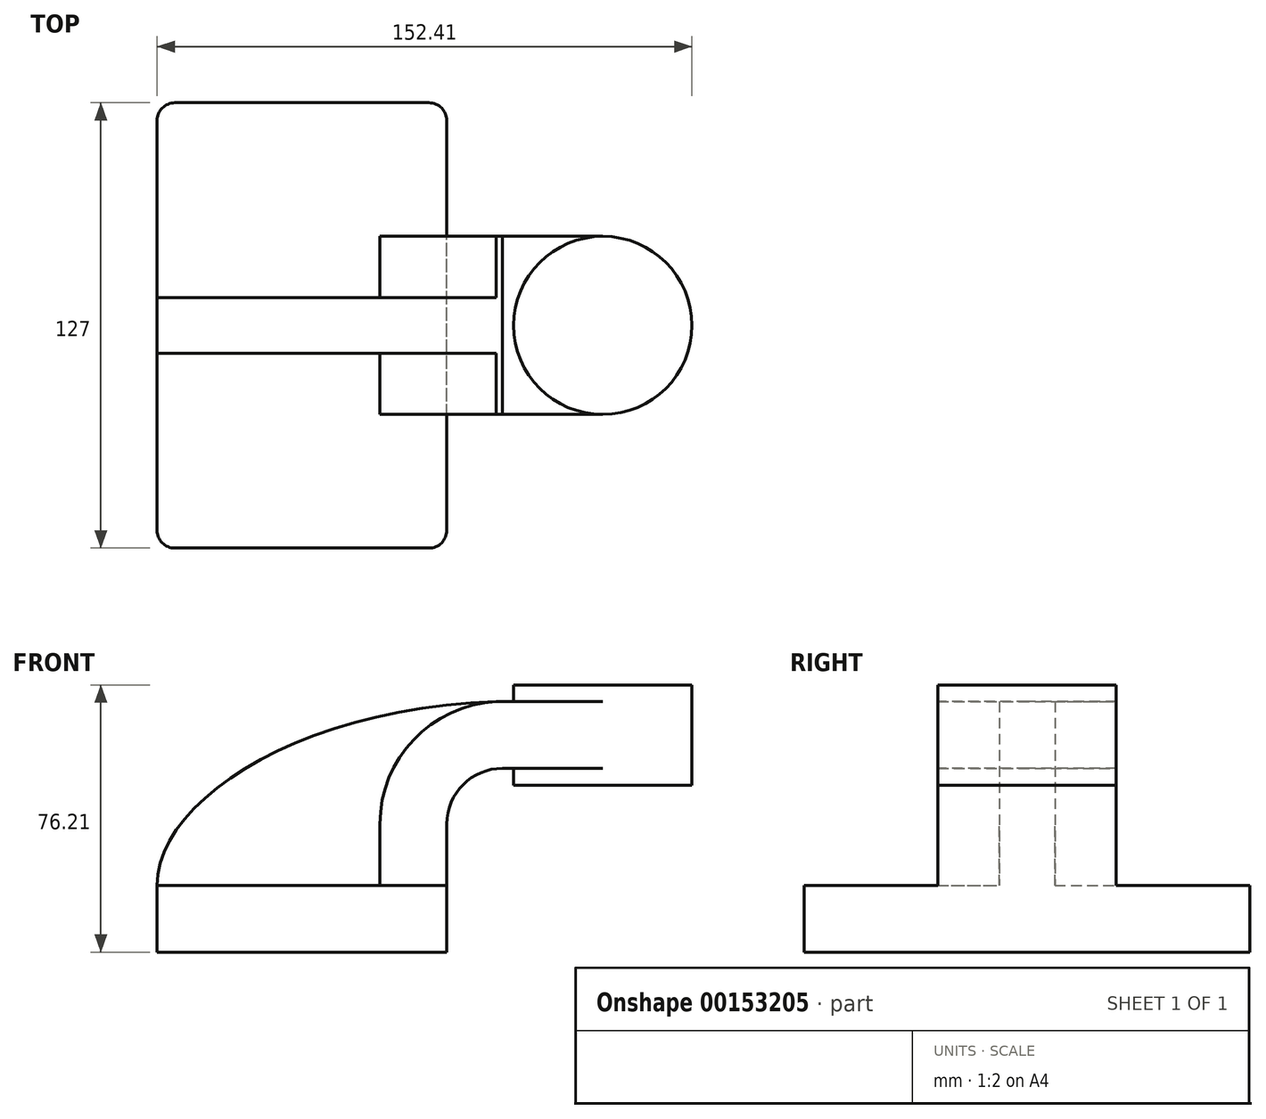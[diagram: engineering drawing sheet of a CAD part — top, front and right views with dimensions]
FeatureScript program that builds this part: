
annotation { "Feature Type Name" : "Feature", "Feature Type Description" : "" }
export const myFeature = defineFeature(function(context is Context, id is Id, definition is map)
    precondition{}
    {
        {
            var Q0;
            Q0=qCreatedBy(makeId("Front.planeOp"),FACE);
            var sketch = newSketch(context, id + "F0", { "sketchPlane" : qUnion([Q0])});
            skLineSegment(sketch, "E0.bottom", {"start": v(41.27, 9.53) * mm, "end": v(-41.28, 9.53) * mm});
            skLineSegment(sketch, "E0.top", {"start": v(41.28, -9.52) * mm, "end": v(-41.27, -9.52) * mm});
            skLineSegment(sketch, "E0.left", {"start": v(41.28, 9.53) * mm, "end": v(41.28, -9.52) * mm});
            skLineSegment(sketch, "E0.right", {"start": v(-41.28, 9.53) * mm, "end": v(-41.27, -9.52) * mm});
            skPoint(sketch, "E0.middle", {"position": v(0, 0) * mm});
            skLineSegment(sketch, "E1.bottom", {"start": v(60.33, 38.1) * mm, "end": v(111.13, 38.1) * mm});
            skLineSegment(sketch, "E1.top", {"start": v(60.33, 66.68) * mm, "end": v(111.13, 66.68) * mm});
            skLineSegment(sketch, "E1.left", {"start": v(60.33, 38.1) * mm, "end": v(60.33, 66.67) * mm});
            skLineSegment(sketch, "E1.right", {"start": v(111.13, 38.1) * mm, "end": v(111.13, 66.68) * mm});
            skPoint(sketch, "E1.middle", {"position": v(85.73, 52.39) * mm});
            skLineSegment(sketch, "E2", {"start": v(41.27, 9.53) * mm, "end": v(41.27, 27) * mm});
            skArc(sketch, "E3", {"start": v(41.28, 27) * mm, "mid": v(45.92, 38.23) * mm, "end": v(57.15, 42.88) * mm});
            skLineSegment(sketch, "E4", {"start": v(57.15, 42.88) * mm, "end": v(85.73, 42.88) * mm});
            skLineSegment(sketch, "E5.0", {"start": v(57.15, 61.93) * mm, "end": v(85.73, 61.93) * mm});
            skArc(sketch, "E5.1", {"start": v(22.23, 27) * mm, "mid": v(32.45, 51.7) * mm, "end": v(57.15, 61.93) * mm});
            skLineSegment(sketch, "E5.2", {"start": v(22.22, 9.53) * mm, "end": v(22.22, 27) * mm});
            skFitSpline(sketch, "E6", {"points": [v(57.15, 61.93) * mm, v(-41.28, 9.53) * mm], "startDerivative": vector(-171.45, -3.59) * mm, "endDerivative": vector(0, -73) * mm});
            skLineSegment(sketch, "E7", {"start": v(85.73, 38.1) * mm, "end": v(85.73, 66.68) * mm});
            skSolve(sketch);
        }
        {
            var Q0;
            Q0=makeQuery(id+"F0.imprint","IMPRINT",FACE,{"disambiguationData":[TD([[makeQuery(id+"F0.imprint","IMPRINT",EDGE,{"derivedFrom":sQuery(id+"F0.wireOp",EDGE,"E0.top")}),-1.0]])]});
            extrude(context, id + "F1", {"entities" : qUnion([Q0]), "endBound" : BoundingType.SYMMETRIC, "depth" : 127 * mm});
        }
        {
            var Q0;
            {var subQ1=sQuery(id+"F0.wireOp",EDGE,"E2");Q0=makeQuery(id+"F0.imprint","IMPRINT",FACE,{"disambiguationData":[TD([[makeQuery(id+"F0.imprint","IMPRINT",EDGE,{"derivedFrom":subQ1}),1.0]])]});}
            extrude(context, id + "F2", {"entities" : qUnion([Q0]), "operationType" : NewBodyOperationType.ADD, "endBound" : BoundingType.SYMMETRIC, "depth" : 50.8 * mm});
        }
        {
            var Q0;
            {var subQ3=sQuery(id+"F0.wireOp",EDGE,"E5.2");Q0=makeQuery(id+"F0.imprint","IMPRINT",FACE,{"disambiguationData":[TD([[makeQuery(id+"F0.imprint","IMPRINT",EDGE,{"derivedFrom":subQ3}),1.0]])]});}
            extrude(context, id + "F3", {"entities" : qUnion([Q0]), "operationType" : NewBodyOperationType.ADD, "endBound" : BoundingType.SYMMETRIC, "depth" : 15.88 * mm});
        }
        {
            var Q0;
            {var subQ0=sQuery(id+"F0.wireOp",EDGE,"E4");var subQ1=sQuery(id+"F0.wireOp",EDGE,"E1.left");var subQ2=makeQuery(id+"F0.imprint","INTERSECT",VERTEX,{"derivedFrom":[subQ1,subQ0]});Q0=makeQuery(id+"F0.imprint","IMPRINT",FACE,{"disambiguationData":[TD([[makeQuery(id+"F0.imprint","IMPRINT",EDGE,{"disambiguationData":[TD([[subQ2,-1.0]])],"derivedFrom":subQ1}),-1.0]])]});}
            extrude(context, id + "F4", {"entities" : qUnion([Q0]), "operationType" : NewBodyOperationType.ADD, "endBound" : BoundingType.SYMMETRIC, "depth" : 50.8 * mm});
        }
        {
            var Q0;
            {var subQ0=sQuery(id+"F0.wireOp",EDGE,"E1.right");Q0=makeQuery(id+"F0.imprint","IMPRINT",FACE,{"disambiguationData":[TD([[makeQuery(id+"F0.imprint","IMPRINT",EDGE,{"derivedFrom":subQ0}),1.0]])]});}
            var Q1;
            Q1=sQuery(id+"F0.wireOp",EDGE,"E7");
            revolve(context, id + "F5", {"operationType" : NewBodyOperationType.ADD, "entities" : qUnion([Q0]), "axis" : qUnion([Q1]), "revolveType" : RevolveType.FULL});
        }
        {
            var Q0;
            Q0=makeQuery(id+"F1.opExtrude","CAP_EDGE",EDGE,{"disambiguationData":[OSD([sQuery(id+"F0.wireOp",EDGE,"E0.left")])],"isStart":false});
            var Q1;
            Q1=makeQuery(id+"F1.opExtrude","CAP_EDGE",EDGE,{"disambiguationData":[OSD([sQuery(id+"F0.wireOp",EDGE,"E0.right")])],"isStart":false});
            var Q2;
            Q2=makeQuery(id+"F1.opExtrude","CAP_EDGE",EDGE,{"disambiguationData":[OSD([sQuery(id+"F0.wireOp",EDGE,"E0.left")])],"isStart":true});
            var Q3;
            Q3=makeQuery(id+"F1.opExtrude","CAP_EDGE",EDGE,{"disambiguationData":[OSD([sQuery(id+"F0.wireOp",EDGE,"E0.right")])],"isStart":true});
            fillet(context, id + "F6", {"entities" : qUnion([Q0, Q1, Q2, Q3]), "radius" : 5.08 * mm, "tangentPropagation" : true, "allowEdgeOverflow" : false});
        }
    });
